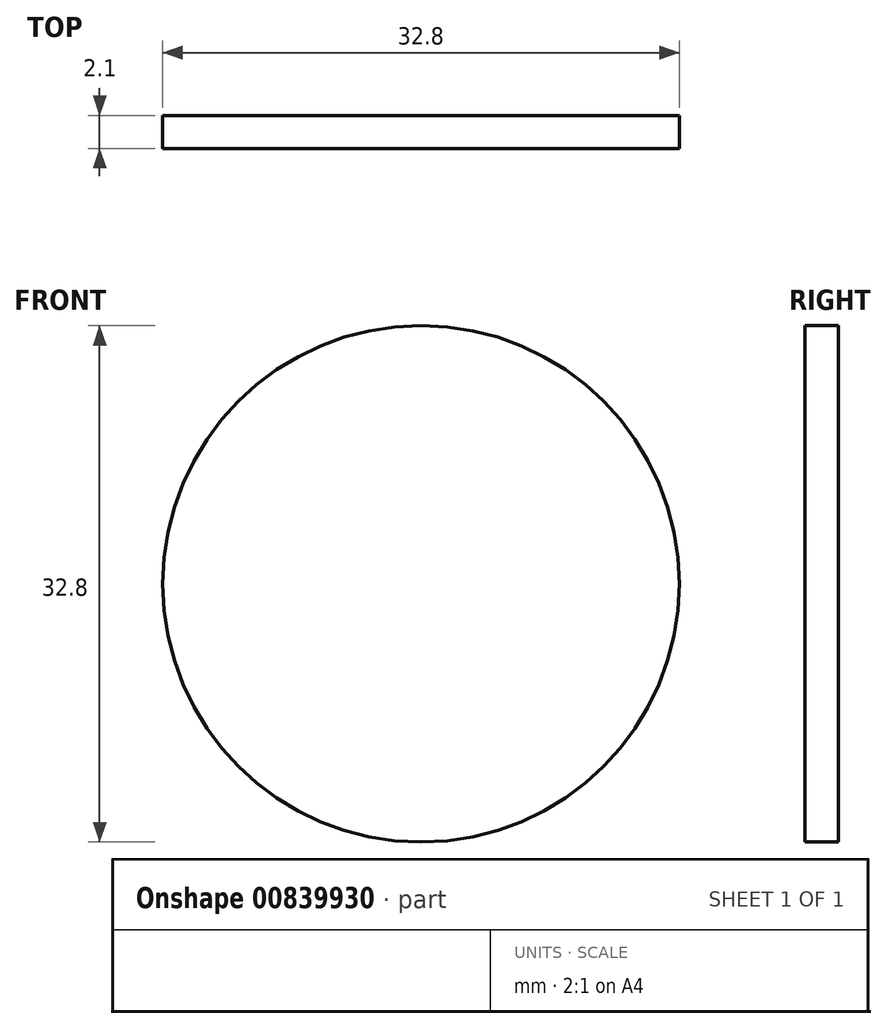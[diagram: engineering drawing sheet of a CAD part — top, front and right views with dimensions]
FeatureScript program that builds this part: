
annotation { "Feature Type Name" : "Feature", "Feature Type Description" : "" }
export const myFeature = defineFeature(function(context is Context, id is Id, definition is map)
    precondition{}
    {
        {
            var Q0;
            Q0=qCreatedBy(makeId("Front.planeOp"),FACE);
            var sketch = newSketch(context, id + "F0", { "sketchPlane" : qUnion([Q0])});
            skCircle(sketch, "E0", {"center": v(0, 0) * mm, "radius": 16.4 * mm});
            skSolve(sketch);
        }
        {
            var Q0;
            Q0=makeQuery(id+"F0.imprint","IMPRINT",FACE,{"disambiguationData":[TD([[makeQuery(id+"F0.imprint","IMPRINT",EDGE,{"derivedFrom":sQuery(id+"F0.wireOp",EDGE,"E0")}),1.0]])]});
            extrude(context, id + "F1", {"entities" : qUnion([Q0]), "depth" : 2.1 * mm, "offsetDistance" : 25 * mm});
        }
    });
